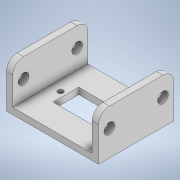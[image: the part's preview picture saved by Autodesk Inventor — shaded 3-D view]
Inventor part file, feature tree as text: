
AUTODESK INVENTOR PART (.ipt)
format: ipt  version: 2021 (Build 250183000, 183)  size: 139,264 bytes
history: native  units: mm
features: sketch x4, extrude x2, hole x2, other x1, fillet x1
ambient origin geometry x8: Origin, YZ Plane, XZ Plane, XY Plane, X Axis, Y Axis, Z Axis, Center Point
bodies: Body1 (feature_tree)
feature tree (10):
  other  "Sólido1"
  extrude  "Extrusión1"  Depth=5.0mm
  fillet  "Empalme1"  Radius=35.0mm
  hole  "Agujero1"  [1 undecoded]
  extrude  "Extrusión2"  [1 undecoded]
  hole  "Agujero2"  [1 undecoded]
  sketch  "Boceto1"  dims[d6=35.0mm d7=0.0mm d8=5.0mm]
  sketch  "Boceto2"  dims[d13=5.0mm d14=6.0mm d15=4.0mm d16=2.0mm d17=90.0deg d18=8.0mm d19=20.594885mm d25=35.0mm d26=0.0mm]
  sketch  "Boceto3"  dims[d32=2.5mm d33=6.0mm d34=4.0mm d35=2.0mm d36=90.0deg d37=8.0mm d38=20.594885mm]
  sketch  "Boceto4"
note: 3 required parameter values undecoded (feature->parameter linkage not recoverable at this tier; creation-order binding heuristic only, values carry confidence <= 0.55)
